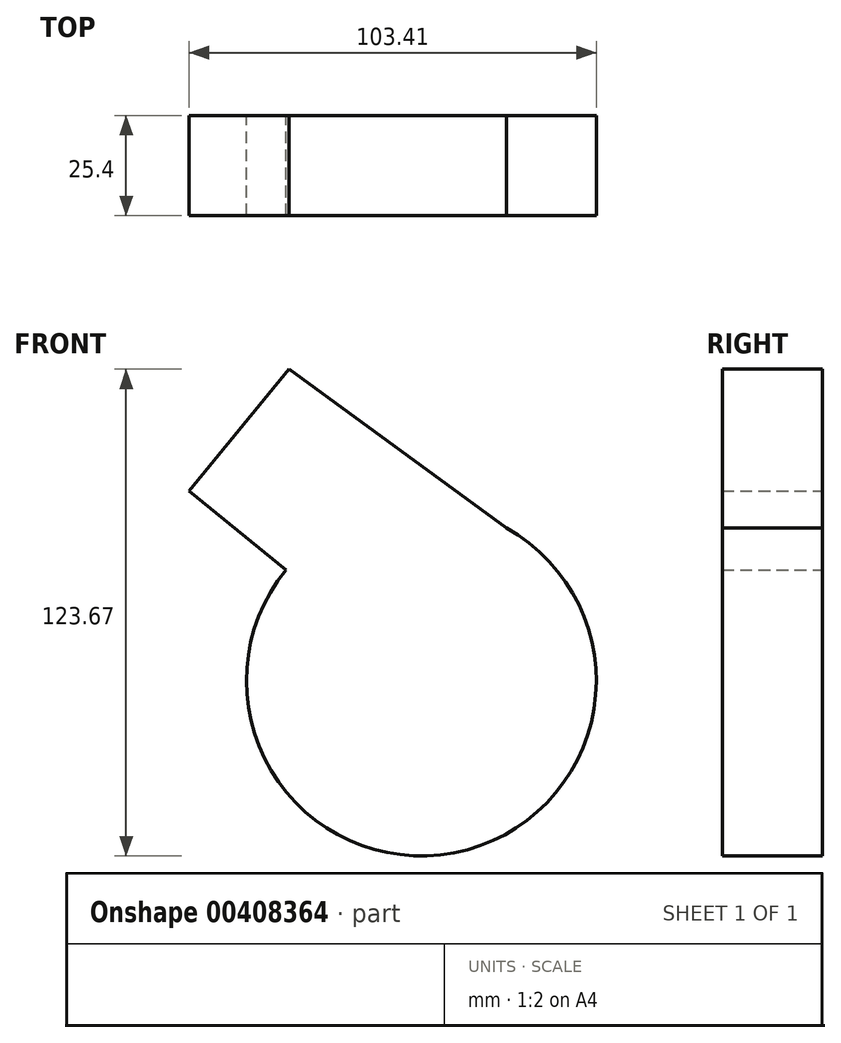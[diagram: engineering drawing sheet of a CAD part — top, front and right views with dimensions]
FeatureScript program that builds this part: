
annotation { "Feature Type Name" : "Feature", "Feature Type Description" : "" }
export const myFeature = defineFeature(function(context is Context, id is Id, definition is map)
    precondition{}
    {
        {
            var Q0;
            Q0=qCreatedBy(makeId("Front.planeOp"),FACE);
            var sketch = newSketch(context, id + "F0", { "sketchPlane" : qUnion([Q0])});
            skLineSegment(sketch, "E0", {"start": v(0, 0) * mm, "end": v(-58.96, 48.28) * mm});
            skCircle(sketch, "E1", {"center": v(0, 0) * mm, "radius": 44.45 * mm});
            skLineSegment(sketch, "E2", {"start": v(-58.96, 48.28) * mm, "end": v(-33.62, 79.22) * mm});
            skLineSegment(sketch, "E3", {"start": v(-33.62, 79.22) * mm, "end": v(30.44, 32.4) * mm});
            skLineSegment(sketch, "E4", {"start": v(30.44, 32.4) * mm, "end": v(0, 0) * mm});
            skSolve(sketch);
        }
        {
            var Q0;
            Q0 = qSketchRegion(id + "F0", true);
            extrude(context, id + "F1", {"entities" : qUnion([Q0]), "depth" : 25.4 * mm});
        }
    });
